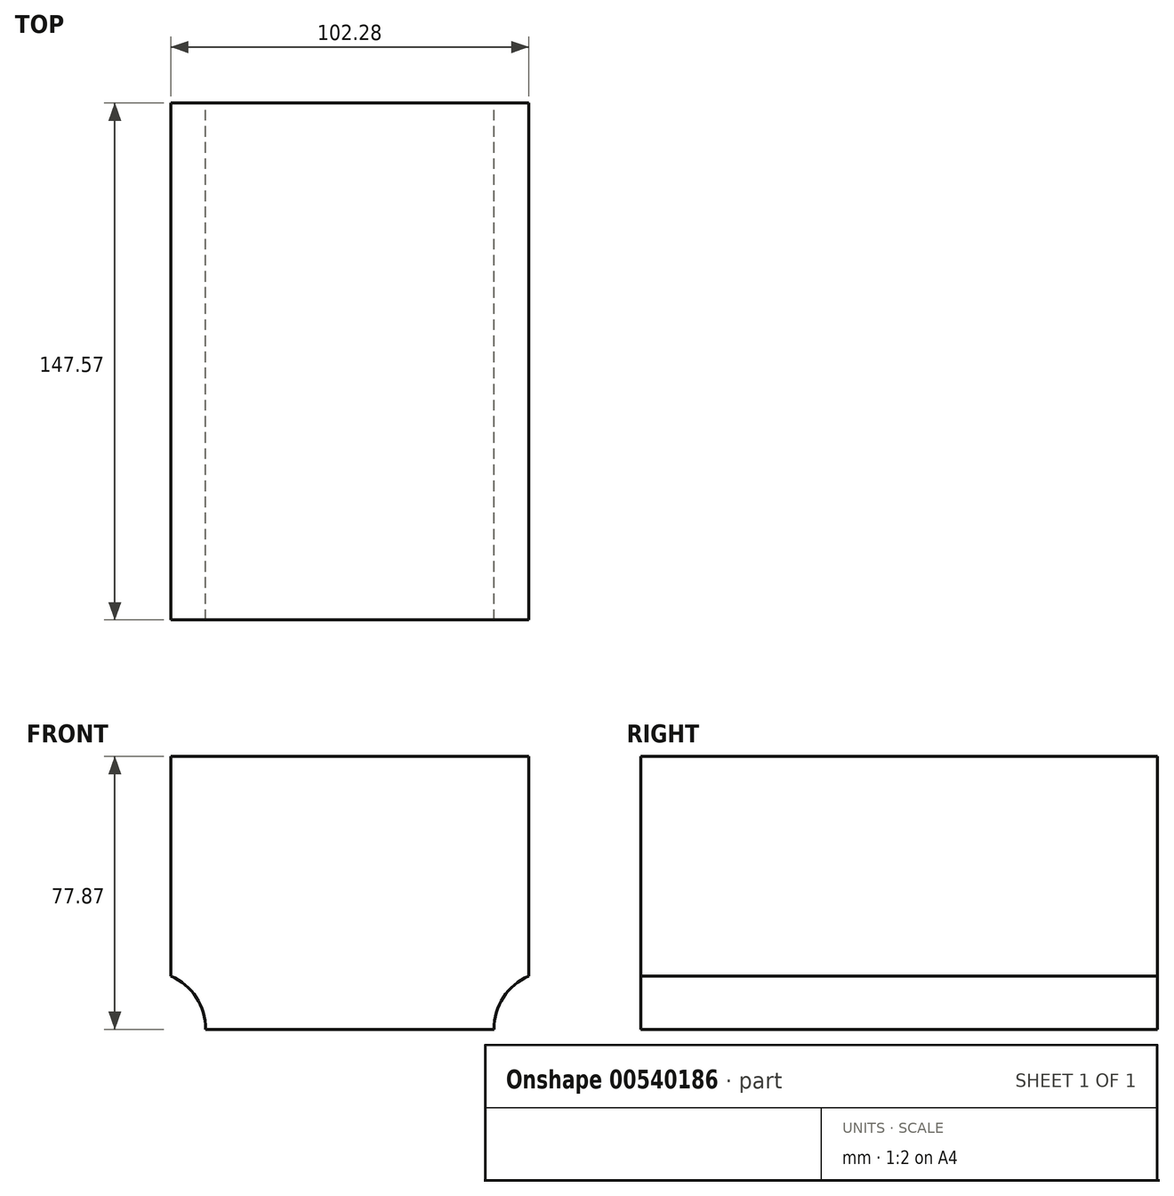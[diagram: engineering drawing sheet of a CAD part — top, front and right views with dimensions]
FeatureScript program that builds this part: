
annotation { "Feature Type Name" : "Feature", "Feature Type Description" : "" }
export const myFeature = defineFeature(function(context is Context, id is Id, definition is map)
    precondition{}
    {
        {
            var Q0;
            Q0=qCreatedBy(makeId("Front.planeOp"),FACE);
            var sketch = newSketch(context, id + "F0", { "sketchPlane" : qUnion([Q0])});
            skCircle(sketch, "E0", {"center": v(-57.74, -46.69) * mm, "radius": 16.57 * mm});
            skLineSegment(sketch, "E1", {"start": v(-63.79, -31.26) * mm, "end": v(-51.14, 0) * mm});
            skLineSegment(sketch, "E2", {"start": v(-51.14, 0) * mm, "end": v(0, 0) * mm});
            skLineSegment(sketch, "E3.MirrorCS", {"start": v(63.79, -31.26) * mm, "end": v(51.14, 0) * mm});
            skLineSegment(sketch, "E4.MirrorCS", {"start": v(51.14, 0) * mm, "end": v(0, 0) * mm});
            skCircle(sketch, "E5.MirrorC", {"center": v(57.74, -46.69) * mm, "radius": 16.57 * mm});
            skLineSegment(sketch, "E6", {"start": v(-57.74, -46.69) * mm, "end": v(57.74, -46.69) * mm});
            skLineSegment(sketch, "E7", {"start": v(63.79, -31.26) * mm, "end": v(57.74, -46.69) * mm});
            skLineSegment(sketch, "E8", {"start": v(-63.79, -31.26) * mm, "end": v(-57.74, -46.69) * mm});
            skLineSegment(sketch, "E9", {"start": v(-51.14, 0) * mm, "end": v(-51.14, 31.18) * mm});
            skLineSegment(sketch, "E10", {"start": v(-51.14, 31.18) * mm, "end": v(51.14, 31.18) * mm});
            skLineSegment(sketch, "E11", {"start": v(51.14, 31.18) * mm, "end": v(51.14, 0) * mm});
            skLineSegment(sketch, "E12", {"start": v(-51.14, 0) * mm, "end": v(-51.14, -46.69) * mm});
            skLineSegment(sketch, "E13", {"start": v(51.14, 0) * mm, "end": v(51.14, -46.69) * mm});
            skSolve(sketch);
        }
        {
            var Q0;
            Q0=makeQuery(id+"F0.imprint","IMPRINT",FACE,{"disambiguationData":[TD([[makeQuery(id+"F0.imprint","IMPRINT",EDGE,{"derivedFrom":sQuery(id+"F0.wireOp",EDGE,"E2")}),1.0]])]});
            var Q1;
            {var subQ6=sQuery(id+"F0.wireOp",EDGE,"E2");Q1=makeQuery(id+"F0.imprint","IMPRINT",FACE,{"disambiguationData":[TD([[makeQuery(id+"F0.imprint","IMPRINT",EDGE,{"derivedFrom":subQ6}),-1.0]])]});}
            extrude(context, id + "F1", {"entities" : qUnion([Q0, Q1]), "depth" : 101.6 * mm, "offsetDistance" : 25.4 * mm, "hasSecondDirection" : true, "secondDirectionOppositeDirection" : true, "secondDirectionDepth" : 45.97 * mm});
        }
    });
